# Revit family: Thorium-Proton
name_source: partatom
category: Furniture
units: mm (PartAtom-declared; Revit-internal decimal feet)

## family parameters
Always vertical = Yes
Cut with Voids When Loaded = No
OmniClass Number = 23.40.10.21.27
OmniClass Title = Exterior Athletic Equipment
Room Calculation Point = No
Shared = No
Work Plane-Based = Yes

## types (2) — shared parameters
Critical falling height (mm) = 1900 mm  [stored 6.2336 ft]
Manufacturer = Sove As
Minimum required safety area (m2) = 53.5
Model name = Thorium Proton
Svanemerke / Nordic EcoLabel = Yes
Type Comments = L=6500, W=7500, H=4400
URL = https://sove.no
zero-valued in all types: Default Elevation

## per-type parameters (varying)
| type | Concrete foundation / Surface mounting | Crossbar 1 | Model | Safety area visibility | Stolpe 110 / 1 |
| Thorium Proton | Yes | Aluminum RAL6018 | 14-200-010 | Yes | Aluminum RAL9022 |
| ChooseYourColor | No | Aluminum RAL-ChooseYourColor | S14-200-010 | No | Aluminum RAL-ChooseYourColor |

note: [stored X ft] marks values corroborated as IEEE doubles in the binary element streams (Revit-internal decimal feet)

## geometry (parser evidence)
native form markers: Sweep x15
no freeform markers — native parametric forms only
